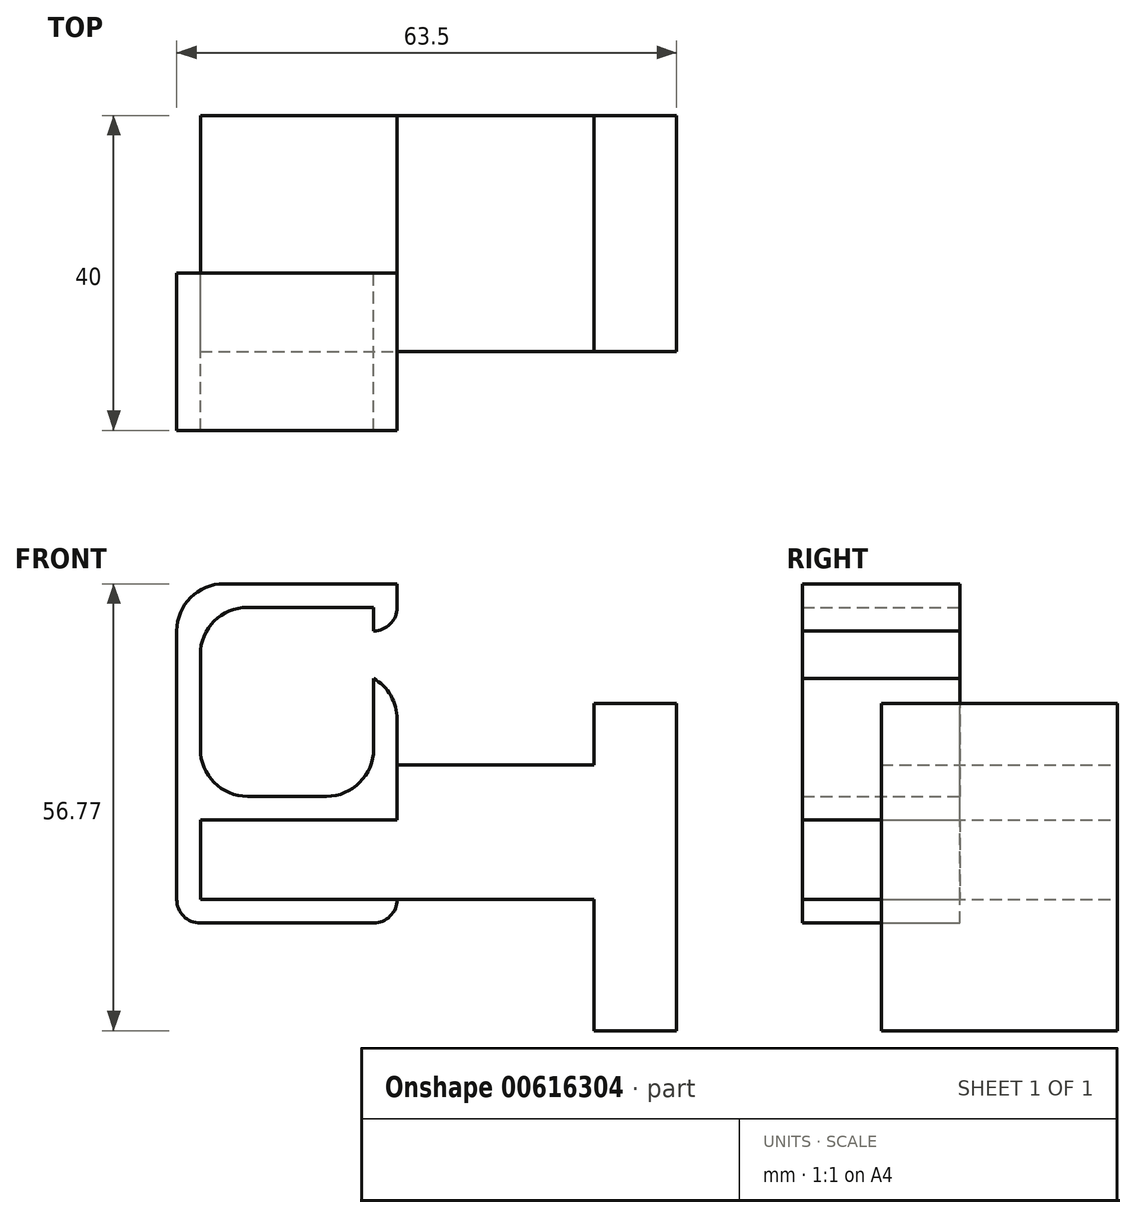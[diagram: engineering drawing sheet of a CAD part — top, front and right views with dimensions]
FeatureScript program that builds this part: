
annotation { "Feature Type Name" : "Feature", "Feature Type Description" : "" }
export const myFeature = defineFeature(function(context is Context, id is Id, definition is map)
    precondition{}
    {
        {
            var Q0;
            Q0=qCreatedBy(makeId("Front.planeOp"),FACE);
            var sketch = newSketch(context, id + "F0", { "sketchPlane" : qUnion([Q0])});
            skLineSegment(sketch, "E0.bottom", {"start": v(-30.5, 5.1) * mm, "end": v(30, 5.1) * mm});
            skLineSegment(sketch, "E0.top", {"start": v(-30.5, -5) * mm, "end": v(30, -5) * mm});
            skLineSegment(sketch, "E0.left", {"start": v(-30.5, 5.1) * mm, "end": v(-30.5, -5) * mm});
            skPoint(sketch, "E0.middle", {"position": v(0, 0) * mm});
            skLineSegment(sketch, "E1.bottom", {"start": v(-5.5, 5.1) * mm, "end": v(30, 5.1) * mm});
            skLineSegment(sketch, "E1.top", {"start": v(-5.5, 12.1) * mm, "end": v(30, 12.1) * mm});
            skLineSegment(sketch, "E1.left", {"start": v(-5.5, 5.1) * mm, "end": v(-5.5, 12.1) * mm});
            skLineSegment(sketch, "E2", {"start": v(19.5, 5.1) * mm, "end": v(19.5, 12.1) * mm});
            skLineSegment(sketch, "E3", {"start": v(30, -5) * mm, "end": v(30, 19.9) * mm});
            skLineSegment(sketch, "E4", {"start": v(30, 19.9) * mm, "end": v(19.5, 19.9) * mm});
            skLineSegment(sketch, "E5", {"start": v(19.5, 19.9) * mm, "end": v(19.5, -5) * mm});
            skLineSegment(sketch, "E6.bottom", {"start": v(19.5, -5) * mm, "end": v(30, -5) * mm});
            skLineSegment(sketch, "E6.top", {"start": v(19.5, -21.67) * mm, "end": v(30, -21.67) * mm});
            skLineSegment(sketch, "E6.left", {"start": v(19.5, -5) * mm, "end": v(19.5, -21.67) * mm});
            skLineSegment(sketch, "E6.right", {"start": v(30, -5) * mm, "end": v(30, -21.67) * mm});
            skSolve(sketch);
        }
        {
            var Q0;
            Q0=qSketchRegion(id+"F0",true);
            extrude(context, id + "F1", {"entities" : qUnion([Q0]), "depth" : 15 * mm, "offsetDistance" : 25 * mm, "hasSecondDirection" : true, "secondDirectionOppositeDirection" : true, "secondDirectionDepth" : 15 * mm});
        }
        {
            var Q0;
            Q0=makeQuery(id+"F1.opExtrude","CAP_FACE",FACE,{"disambiguationData":[OSD([sQuery(id+"F0.wireOp",EDGE,"E0.bottom"),sQuery(id+"F0.wireOp",EDGE,"E0.top"),sQuery(id+"F0.wireOp",EDGE,"E0.left"),sQuery(id+"F0.wireOp",EDGE,"E1.top"),sQuery(id+"F0.wireOp",EDGE,"E1.left"),sQuery(id+"F0.wireOp",EDGE,"E3"),sQuery(id+"F0.wireOp",EDGE,"E4"),sQuery(id+"F0.wireOp",EDGE,"E5")])],"isStart":false});
            var sketch = newSketch(context, id + "F2", { "sketchPlane" : qUnion([Q0])});
            skLineSegment(sketch, "E7.0", {"start": v(-30.5, 5.1) * mm, "end": v(-5.5, 5.1) * mm});
            skLineSegment(sketch, "E8.0", {"start": v(-30.5, 5.1) * mm, "end": v(-30.5, -5) * mm});
            skLineSegment(sketch, "E9.0", {"start": v(-5.5, 5.1) * mm, "end": v(-5.5, 12.1) * mm});
            skLineSegment(sketch, "E10.0", {"start": v(-33.5, 8.1) * mm, "end": v(-33.5, -5) * mm});
            skLineSegment(sketch, "E10.1", {"start": v(-30.5, 8.1) * mm, "end": v(-8.5, 8.1) * mm});
            skLineSegment(sketch, "E10.5", {"start": v(-8.5, 8.1) * mm, "end": v(-8.5, 15.1) * mm});
            skLineSegment(sketch, "E11.0", {"start": v(-30.5, -5) * mm, "end": v(-5.5, -5) * mm});
            skLineSegment(sketch, "E12.0", {"start": v(32.5, -8) * mm, "end": v(32.5, 15) * mm, "construction": true});
            skLineSegment(sketch, "E12.1", {"start": v(-30.5, -8) * mm, "end": v(-5.5, -8) * mm, "construction": true});
            skLineSegment(sketch, "E13", {"start": v(-33.5, -5) * mm, "end": v(-33.5, -8) * mm});
            skLineSegment(sketch, "E14", {"start": v(-33.5, -8) * mm, "end": v(-5.5, -8) * mm});
            skLineSegment(sketch, "E15", {"start": v(9.5, -5) * mm, "end": v(-30.5, -5) * mm});
            skPoint(sketch, "E16.0.start.orphan", {"position": v(-30.5, -5) * mm});
            skLineSegment(sketch, "E17", {"start": v(-33.5, 8.1) * mm, "end": v(-33.5, 35.1) * mm});
            skLineSegment(sketch, "E18.1", {"start": v(-30.5, 8.1) * mm, "end": v(-30.5, 32.1) * mm});
            skLineSegment(sketch, "E19", {"start": v(-5.5, 12.1) * mm, "end": v(-5.5, 23.1) * mm});
            skLineSegment(sketch, "E20", {"start": v(-8.5, 23.1) * mm, "end": v(-8.5, 15.1) * mm});
            skLineSegment(sketch, "E21", {"start": v(-5.5, -5) * mm, "end": v(-5.5, -8) * mm});
            skLineSegment(sketch, "E22.trimOffspring", {"start": v(9.5, -8) * mm, "end": v(32.5, -8) * mm, "construction": true});
            skLineSegment(sketch, "E23", {"start": v(-30.5, 32.1) * mm, "end": v(-5.5, 32.1) * mm});
            skLineSegment(sketch, "E24", {"start": v(-5.5, 32.1) * mm, "end": v(-5.5, 35.1) * mm});
            skLineSegment(sketch, "E25", {"start": v(-5.5, 35.1) * mm, "end": v(-33.5, 35.1) * mm});
            skLineSegment(sketch, "E26", {"start": v(-8.5, 23.1) * mm, "end": v(-5.5, 23.1) * mm});
            skLineSegment(sketch, "E27.bottom", {"start": v(-5.5, 32.1) * mm, "end": v(-8.5, 32.1) * mm});
            skLineSegment(sketch, "E27.top", {"start": v(-5.5, 29.1) * mm, "end": v(-8.5, 29.1) * mm});
            skLineSegment(sketch, "E27.left", {"start": v(-5.5, 32.1) * mm, "end": v(-5.5, 29.1) * mm});
            skLineSegment(sketch, "E27.right", {"start": v(-8.5, 32.1) * mm, "end": v(-8.5, 29.1) * mm});
            skPoint(sketch, "E28.orphan", {"position": v(-8.5, 27.1) * mm});
            skPoint(sketch, "E29.orphan", {"position": v(-5.5, 27.1) * mm});
            skSolve(sketch);
        }
        {
            var Q0;
            Q0=qSketchRegion(id+"F2",true);
            extrude(context, id + "F3", {"entities" : qUnion([Q0]), "depth" : 10 * mm, "offsetDistance" : 25 * mm, "hasSecondDirection" : true, "secondDirectionOppositeDirection" : true, "secondDirectionDepth" : 10 * mm});
        }
        {
            var Q0;
            Q0=makeQuery(id+"F3.opExtrude","SWEPT_EDGE",EDGE,{"disambiguationData":[OSD([sQuery(id+"F2.wireOp",EDGE,"E10.1"),sQuery(id+"F2.wireOp",EDGE,"E18.1")])]});
            var Q1;
            Q1=makeQuery(id+"F3.opExtrude","SWEPT_EDGE",EDGE,{"disambiguationData":[OSD([sQuery(id+"F2.wireOp",EDGE,"E18.0"),sQuery(id+"F2.wireOp",EDGE,"E18.1")])]});
            var Q2;
            Q2=makeQuery(id+"F3.opExtrude","SWEPT_EDGE",EDGE,{"disambiguationData":[OSD([sQuery(id+"F2.wireOp",EDGE,"E10.1"),sQuery(id+"F2.wireOp",EDGE,"E10.5")])]});
            var Q3;
            Q3=makeQuery(id+"F3.opExtrude","SWEPT_EDGE",EDGE,{"disambiguationData":[OSD([sQuery(id+"F2.wireOp",EDGE,"E10.3"),sQuery(id+"F2.wireOp",EDGE,"E10.4")])]});
            var Q4;
            Q4=makeQuery(id+"F3.opExtrude","SWEPT_EDGE",EDGE,{"disambiguationData":[OSD([sQuery(id+"F2.wireOp",EDGE,"E17"),sQuery(id+"F2.wireOp",EDGE,"gKanQStJ-fhQx-XZDo-CAxQ-tm1A6QolvCmM")])]});
            var Q5;
            Q5=makeQuery(id+"F3.opExtrude","SWEPT_EDGE",EDGE,{"disambiguationData":[OSD([sQuery(id+"F2.wireOp",EDGE,"E10.4"),sQuery(id+"F2.wireOp",EDGE,"E19")])]});
            fillet(context, id + "F4", {"entities" : qUnion([Q0, Q1, Q2, Q3, Q4, Q5]), "radius" : 6 * mm, "tangentPropagation" : true, "allowEdgeOverflow" : false});
        }
        {
            var Q0;
            Q0=makeQuery(id+"F3.opExtrude","SWEPT_EDGE",EDGE,{"disambiguationData":[OSD([sQuery(id+"F2.wireOp",EDGE,"E13"),sQuery(id+"F2.wireOp",EDGE,"E14")])]});
            var Q1;
            Q1=makeQuery(id+"F3.opExtrude","SWEPT_EDGE",EDGE,{"disambiguationData":[OSD([sQuery(id+"F2.wireOp",EDGE,"E14"),sQuery(id+"F2.wireOp",EDGE,"10UTMtSn-Xdb9-fhmc-p5Ld-yhSijxxTlpbN")])]});
            var Q2;
            Q2=makeQuery(id+"F3.opExtrude","SWEPT_EDGE",EDGE,{"disambiguationData":[OSD([sQuery(id+"F2.wireOp",EDGE,"umD0eQzf-GjOD-i8nX-VY2R-4t68M5MixWvP"),sQuery(id+"F2.wireOp",EDGE,"TDOxhsxO-41ug-WlRz-RTQR-re5DJAkylYrA")])]});
            var Q3;
            Q3=makeQuery(id+"F3.opExtrude","SWEPT_EDGE",EDGE,{"disambiguationData":[OSD([sQuery(id+"F2.wireOp",EDGE,"E27.top"),sQuery(id+"F2.wireOp",EDGE,"E27.left")])]});
            fillet(context, id + "F5", {"entities" : qUnion([Q0, Q1, Q2, Q3]), "radius" : 3 * mm, "tangentPropagation" : true, "allowEdgeOverflow" : false});
        }
    });
